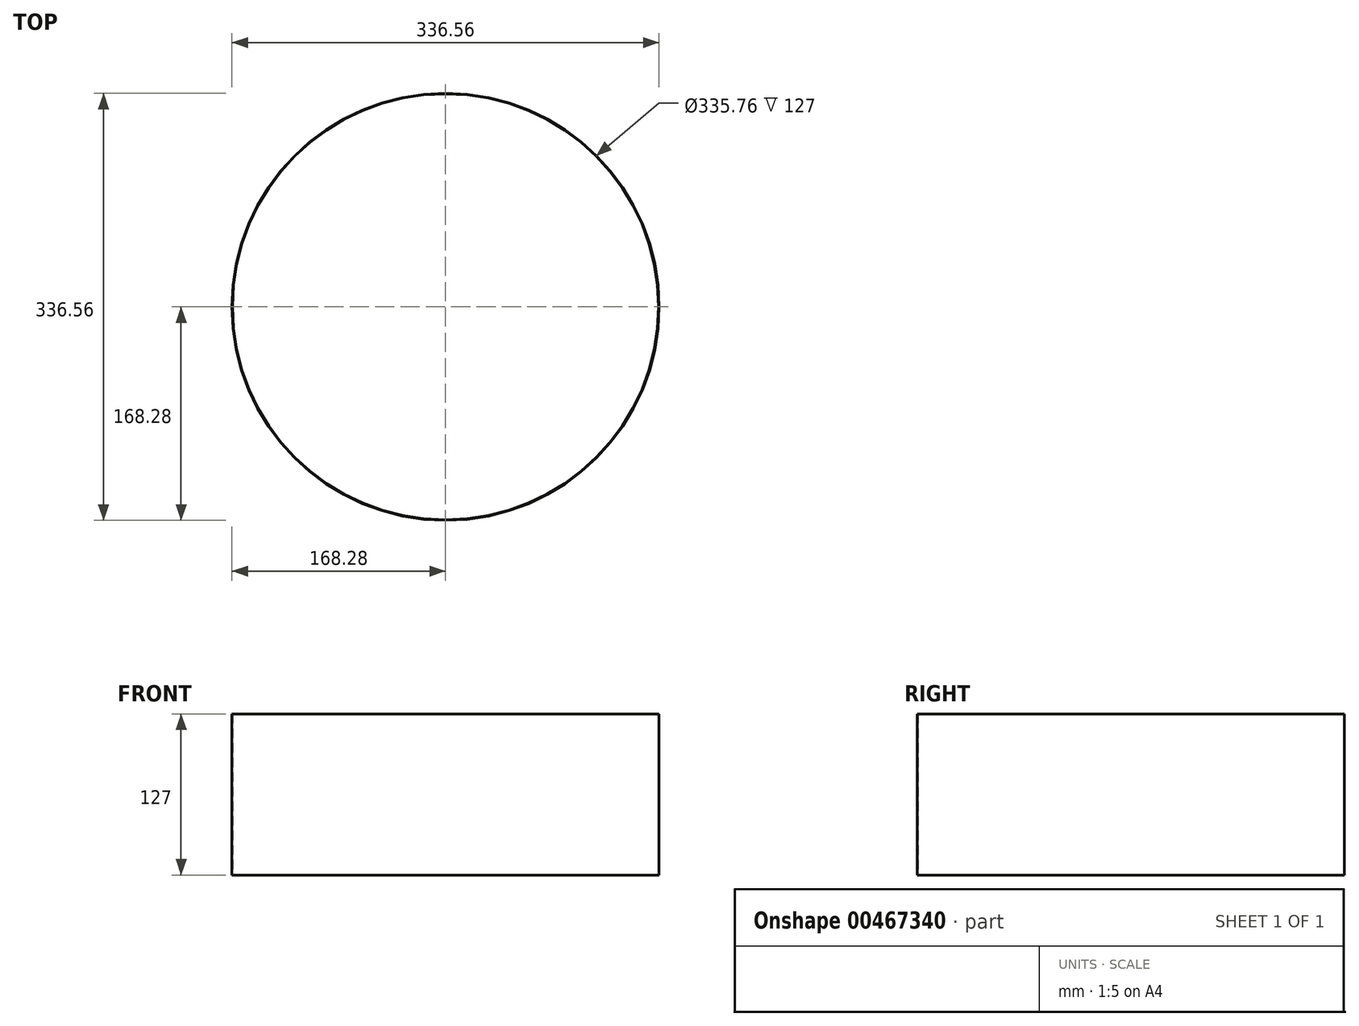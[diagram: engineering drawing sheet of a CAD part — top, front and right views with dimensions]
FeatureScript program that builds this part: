
annotation { "Feature Type Name" : "Feature", "Feature Type Description" : "" }
export const myFeature = defineFeature(function(context is Context, id is Id, definition is map)
    precondition{}
    {
        {
            var Q0;
            Q0=qCreatedBy(makeId("Top.planeOp"),FACE);
            var sketch = newSketch(context, id + "F0", { "sketchPlane" : qUnion([Q0])});
            skCircle(sketch, "E0", {"center": v(0, 0) * mm, "radius": 167.88 * mm});
            skCircle(sketch, "E1", {"center": v(0, 0) * mm, "radius": 168.28 * mm});
            skSolve(sketch);
        }
        {
            var Q0;
            Q0=makeQuery(id+"F0.imprint","IMPRINT",FACE,{"disambiguationData":[TD([[makeQuery(id+"F0.imprint","IMPRINT",EDGE,{"derivedFrom":sQuery(id+"F0.wireOp",EDGE,"E0")}),-1.0]])]});
            extrude(context, id + "F1", {"entities" : qUnion([Q0]), "depth" : 127 * mm});
        }
    });
